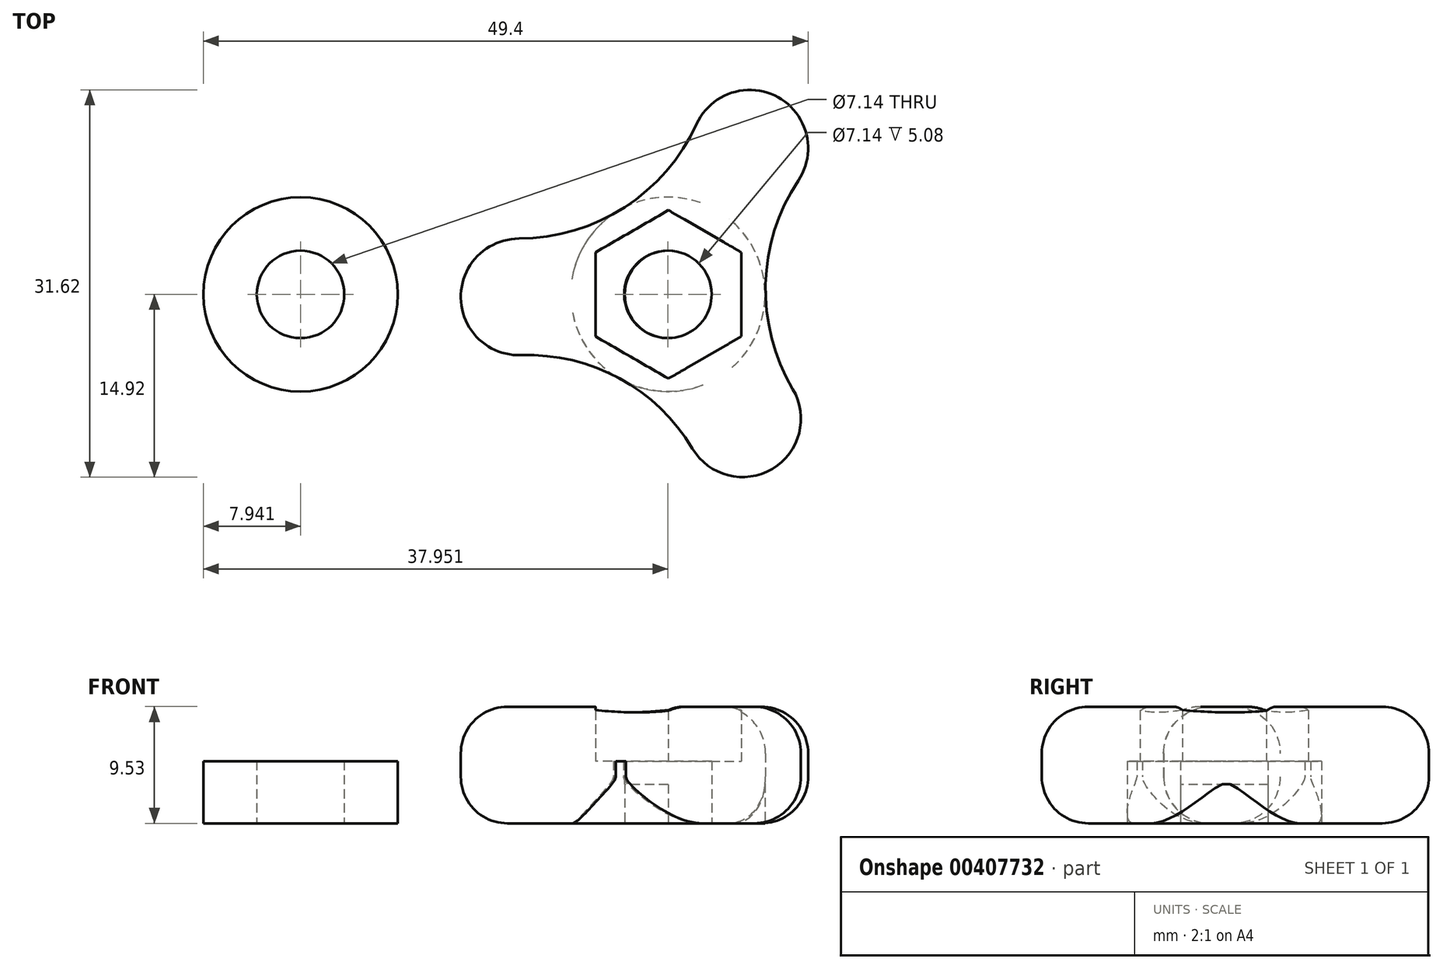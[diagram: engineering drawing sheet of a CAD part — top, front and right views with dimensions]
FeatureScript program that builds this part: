
annotation { "Feature Type Name" : "Feature", "Feature Type Description" : "" }
export const myFeature = defineFeature(function(context is Context, id is Id, definition is map)
    precondition{}
    {
        {
            var Q0;
            Q0=qCreatedBy(makeId("Top.planeOp"),FACE);
            var sketch = newSketch(context, id + "F0", { "sketchPlane" : qUnion([Q0])});
            skCircle(sketch, "E0.cCircle", {"center": v(15.67, 0) * mm, "radius": 7.94 * mm, "construction": true});
            skPoint(sketch, "E0.0.midPoint", {"position": v(23.61, 0) * mm});
            skArc(sketch, "E1", {"start": v(26.29, 9.3) * mm, "mid": v(24.63, 16.1) * mm, "end": v(17.99, 13.92) * mm});
            skArc(sketch, "E2", {"start": v(17.64, -12.6) * mm, "mid": v(24.16, -14.25) * mm, "end": v(25.83, -7.74) * mm});
            skArc(sketch, "E3", {"start": v(3.45, 4.56) * mm, "mid": v(-1.29, -0.3) * mm, "end": v(3.64, -4.97) * mm});
            skArc(sketch, "E4", {"start": v(3.45, 4.56) * mm, "mid": v(12.1, 7.12) * mm, "end": v(17.99, 13.92) * mm});
            skPoint(sketch, "E4.first.point", {"position": v(3.45, 4.56) * mm});
            skPoint(sketch, "E4.second.point", {"position": v(11.42, 6.7) * mm});
            skPoint(sketch, "E4.third.point", {"position": v(17.99, 13.92) * mm});
            skArc(sketch, "E5", {"start": v(26.29, 9.3) * mm, "mid": v(23.61, 0.85) * mm, "end": v(25.83, -7.74) * mm});
            skPoint(sketch, "E5.first.point", {"position": v(26.29, 9.3) * mm});
            skPoint(sketch, "E5.third.point", {"position": v(25.83, -7.74) * mm});
            skArc(sketch, "E6", {"start": v(17.64, -12.6) * mm, "mid": v(11.68, -6.86) * mm, "end": v(3.64, -4.97) * mm});
            skPoint(sketch, "E6.first.point", {"position": v(17.64, -12.6) * mm});
            skPoint(sketch, "E6.second.point", {"position": v(12.02, -7.05) * mm});
            skPoint(sketch, "E6.third.point", {"position": v(3.64, -4.97) * mm});
            skCircle(sketch, "E7.cCircle", {"center": v(15.67, 0) * mm, "radius": 5.95 * mm, "construction": true});
            skLineSegment(sketch, "E7.0", {"start": v(21.63, 3.44) * mm, "end": v(21.63, -3.44) * mm});
            skLineSegment(sketch, "E7.1", {"start": v(21.63, -3.44) * mm, "end": v(15.67, -6.87) * mm});
            skLineSegment(sketch, "E7.2", {"start": v(15.67, -6.87) * mm, "end": v(9.72, -3.44) * mm});
            skLineSegment(sketch, "E7.3", {"start": v(9.72, -3.44) * mm, "end": v(9.72, 3.44) * mm});
            skLineSegment(sketch, "E7.4", {"start": v(9.72, 3.44) * mm, "end": v(15.67, 6.87) * mm});
            skLineSegment(sketch, "E7.5", {"start": v(15.67, 6.87) * mm, "end": v(21.63, 3.44) * mm});
            skPoint(sketch, "E7.0.midPoint", {"position": v(21.63, 0) * mm});
            skCircle(sketch, "E8", {"center": v(15.67, 0) * mm, "radius": 3.57 * mm});
            skSolve(sketch);
        }
        {
            var Q0;
            Q0=makeQuery(id+"F0.imprint","IMPRINT",FACE,{"disambiguationData":[TD([[makeQuery(id+"F0.imprint","IMPRINT",EDGE,{"derivedFrom":sQuery(id+"F0.wireOp",EDGE,"E1")}),1.0]])]});
            extrude(context, id + "F1", {"entities" : qUnion([Q0]), "depth" : 9.52 * mm, "offsetDistance" : 25.4 * mm});
        }
        {
            var Q0;
            Q0=makeQuery(id+"F0.imprint","IMPRINT",FACE,{"disambiguationData":[TD([[makeQuery(id+"F0.imprint","IMPRINT",EDGE,{"derivedFrom":sQuery(id+"F0.wireOp",EDGE,"E7.0")}),-1.0]])]});
            extrude(context, id + "F2", {"entities" : qUnion([Q0]), "operationType" : NewBodyOperationType.ADD, "depth" : 3.17 * mm, "offsetDistance" : 25.4 * mm});
        }
        {
            var Q0;
            Q0=makeQuery(id+"F1.opExtrude","CAP_EDGE",EDGE,{"disambiguationData":[OSD([sQuery(id+"F0.wireOp",EDGE,"E6")])],"isStart":false});
            var Q1;
            Q1=makeQuery(id+"F1.opExtrude","CAP_EDGE",EDGE,{"disambiguationData":[OSD([sQuery(id+"F0.wireOp",EDGE,"E6")])],"isStart":true});
            fillet(context, id + "F3", {"entities" : qUnion([Q0, Q1]), "radius" : 3.8 * mm, "tangentPropagation" : true, "allowEdgeOverflow" : false});
        }
        {
            var Q0;
            Q0=makeQuery(id+"F0.imprint","IMPRINT",FACE,{"disambiguationData":[TD([[makeQuery(id+"F0.imprint","IMPRINT",EDGE,{"derivedFrom":sQuery(id+"F0.wireOp",EDGE,"E7.0")}),-1.0]])]});
            var sketch = newSketch(context, id + "F4", { "sketchPlane" : qUnion([Q0])});
            skCircle(sketch, "E9", {"center": v(15.63, 0) * mm, "radius": 7.94 * mm});
            skCircle(sketch, "E10", {"center": v(15.63, 0) * mm, "radius": 3.57 * mm});
            skSolve(sketch);
        }
        {
            var Q0;
            Q0 = qSketchRegion(id + "F4", true);
            extrude(context, id + "F5", {"entities" : qUnion([Q0]), "operationType" : NewBodyOperationType.ADD, "depth" : 5.08 * mm, "offsetDistance" : 25.4 * mm});
        }
        {
            var Q0;
            Q0=qCreatedBy(makeId("Top.planeOp"),FACE);
            var sketch = newSketch(context, id + "F6", { "sketchPlane" : qUnion([Q0])});
            skCircle(sketch, "E11", {"center": v(-14.38, 0) * mm, "radius": 7.94 * mm});
            skCircle(sketch, "E12", {"center": v(-14.38, 0) * mm, "radius": 3.57 * mm});
            skSolve(sketch);
        }
        {
            var Q0;
            Q0=makeQuery(id+"F6.imprint","IMPRINT",FACE,{"disambiguationData":[TD([[makeQuery(id+"F6.imprint","IMPRINT",EDGE,{"derivedFrom":sQuery(id+"F6.wireOp",EDGE,"E11")}),1.0]])]});
            extrude(context, id + "F7", {"entities" : qUnion([Q0]), "depth" : 5.08 * mm, "offsetDistance" : 25.4 * mm});
        }
    });
